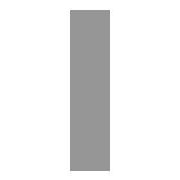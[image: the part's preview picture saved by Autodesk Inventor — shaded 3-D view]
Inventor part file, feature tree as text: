
AUTODESK INVENTOR PART (.ipt)
format: ipt  version: 2019.4 (Build 234330000, 330)  size: 115,712 bytes
history: native  units: mm (DEFAULTED — no unit token found)
features: other x4, plane x3, split x2, sketch x2
ambient origin geometry x8: Origin, YZ Plane, XZ Plane, XY Plane, X Axis, Y Axis, Z Axis, Center Point
bodies: Solid1 (feature_tree), Body (feature_tree)
feature tree (11):
  parser-record x1  (decoder bookkeeping rows leaked as tree rows — omitted from the tree; the rows remain in map.json)
  other  "Driven Length"
  other  "Start plane"
  other  "End plane"
  plane  "Work Plane7"
  split  "Split4"
  plane  "Work Plane8"
  split  "Split5"
  sketch  "Sketch3"  dims[d0=12.7mm]
  plane  "Work Plane3"
  sketch  "Sketch4"  dims[d1=9.525mm d2=471.380039mm d3=0.0mm d4=4.7625mm d5=6.35mm d6=6.760624mm d7=478.140663mm d8=90.0deg d9=471.380039mm]
